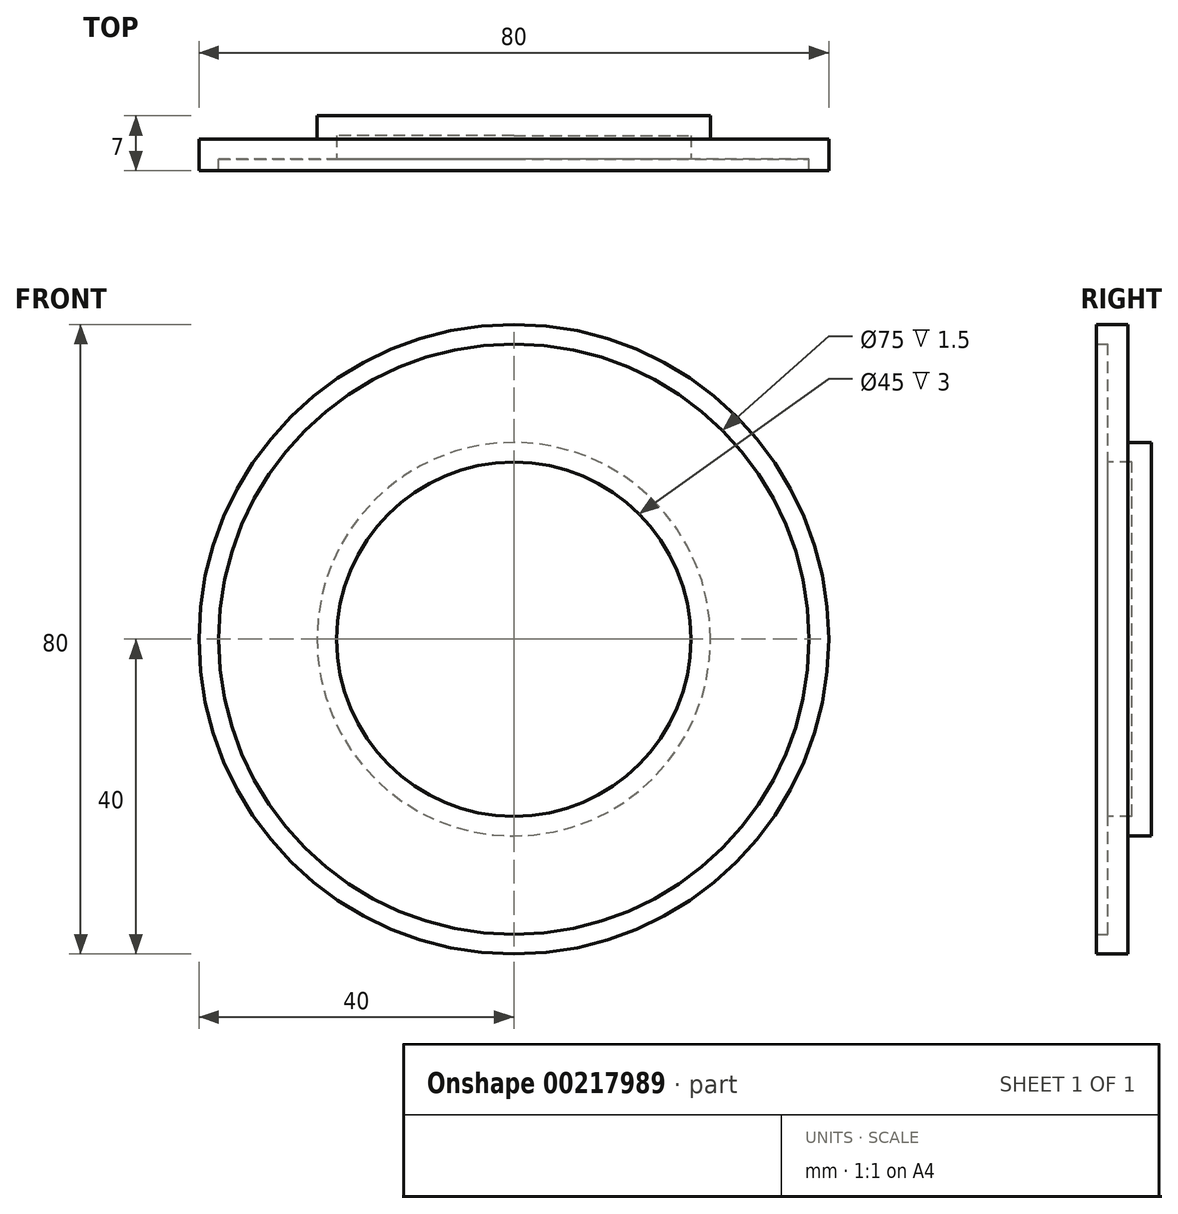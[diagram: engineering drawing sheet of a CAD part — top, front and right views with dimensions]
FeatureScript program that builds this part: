
annotation { "Feature Type Name" : "Feature", "Feature Type Description" : "" }
export const myFeature = defineFeature(function(context is Context, id is Id, definition is map)
    precondition{}
    {
        {
            var Q0;
            Q0=qCreatedBy(makeId("Front.planeOp"),FACE);
            var sketch = newSketch(context, id + "F0", { "sketchPlane" : qUnion([Q0])});
            skCircle(sketch, "E0", {"center": v(0, 0) * mm, "radius": 40 * mm});
            skSolve(sketch);
        }
        {
            var Q0;
            Q0=makeQuery(id+"F0.imprint","IMPRINT",FACE,{"disambiguationData":[TD([[makeQuery(id+"F0.imprint","IMPRINT",EDGE,{"derivedFrom":sQuery(id+"F0.wireOp",EDGE,"E0")}),1.0]])]});
            extrude(context, id + "F1", {"entities" : qUnion([Q0]), "depth" : 3 * mm});
        }
        {
            var Q0;
            Q0=qSketchRegion(id+"F0",true);
            var Q1;
            Q1=makeQuery(id+"F1.opExtrude","CAP_FACE",FACE,{"disambiguationData":[OSD([sQuery(id+"F0.wireOp",EDGE,"E0")])],"isStart":false});
            extrude(context, id + "F2", {"entities" : qUnion([Q0, Q1]), "operationType" : NewBodyOperationType.ADD, "depth" : 1 * mm});
        }
        {
            var Q0;
            Q0=makeQuery(id+"F1.opExtrude","CAP_FACE",FACE,{"disambiguationData":[OSD([sQuery(id+"F0.wireOp",EDGE,"E0")])],"isStart":true});
            var sketch = newSketch(context, id + "F3", { "sketchPlane" : qUnion([Q0])});
            skCircle(sketch, "E1", {"center": v(0, 0) * mm, "radius": 25 * mm});
            skSolve(sketch);
        }
        {
            var Q0;
            Q0=makeQuery(id+"F3.imprint","IMPRINT",FACE,{"disambiguationData":[TD([[makeQuery(id+"F3.imprint","IMPRINT",EDGE,{"derivedFrom":sQuery(id+"F3.wireOp",EDGE,"E1")}),1.0]])]});
            extrude(context, id + "F4", {"entities" : qUnion([Q0]), "operationType" : NewBodyOperationType.ADD, "depth" : 3 * mm});
        }
        {
            var Q0;
            {var subQ0=sQuery(id+"F0.wireOp",EDGE,"E0");Q0=makeQuery(id+"F2.opExtrude","CAP_FACE",FACE,{"disambiguationData":[OSD([subQ0]),TDD([makeQuery(id+"F1.opExtrude","CAP_FACE",FACE,{"disambiguationData":[OSD([subQ0])],"isStart":false})])],"isStart":false});}
            shell(context, id + "F5", {"entities" : qUnion([Q0]), "thickness" : 2.5 * mm});
        }
    });
